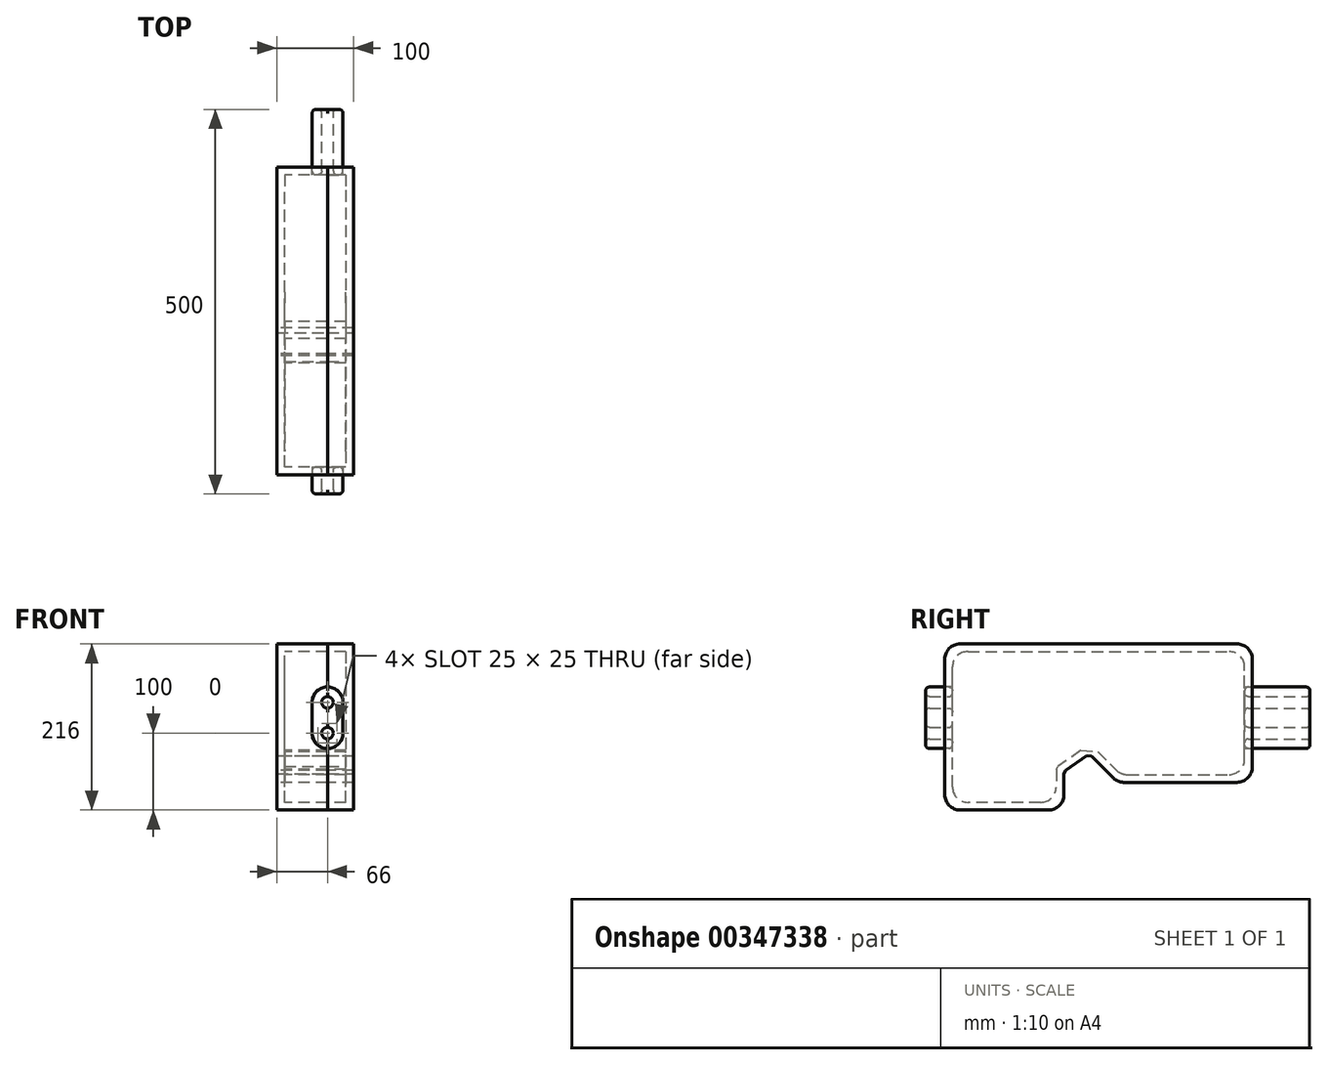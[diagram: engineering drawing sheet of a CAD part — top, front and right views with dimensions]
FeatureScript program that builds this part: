
annotation { "Feature Type Name" : "Feature", "Feature Type Description" : "" }
export const myFeature = defineFeature(function(context is Context, id is Id, definition is map)
    precondition{}
    {
        {
            var Q0;
            Q0=qCreatedBy(makeId("Right.planeOp"),FACE);
            var sketch = newSketch(context, id + "F0", { "sketchPlane" : qUnion([Q0])});
            skLineSegment(sketch, "E0.bottom", {"start": v(200, 75) * mm, "end": v(-200, 75) * mm});
            skLineSegment(sketch, "E0.left", {"start": v(200, 75) * mm, "end": v(200, -75) * mm});
            skLineSegment(sketch, "E0.right", {"start": v(-200, 75) * mm, "end": v(-200, -75) * mm});
            skPoint(sketch, "E0.middle", {"position": v(0, 0) * mm});
            skLineSegment(sketch, "E1", {"start": v(-200, -75) * mm, "end": v(-200, -141) * mm});
            skLineSegment(sketch, "E2", {"start": v(-200, -141) * mm, "end": v(-45, -141) * mm});
            skLineSegment(sketch, "E3", {"start": v(-45, -141) * mm, "end": v(-45, -91) * mm});
            skLineSegment(sketch, "E4", {"start": v(-12.23, -68.06) * mm, "end": v(-87.83, -68.06) * mm, "construction": true});
            skLineSegment(sketch, "E5", {"start": v(200, -75) * mm, "end": v(200, -105) * mm});
            skLineSegment(sketch, "E6", {"start": v(200, -105) * mm, "end": v(25, -105) * mm});
            skLineSegment(sketch, "E7", {"start": v(25, -105) * mm, "end": v(-12.23, -68.06) * mm});
            skLineSegment(sketch, "E8", {"start": v(-45, -91) * mm, "end": v(-12.23, -68.06) * mm});
            skSolve(sketch);
        }
        {
            var Q0;
            Q0=makeQuery(id+"F0.imprint","IMPRINT",FACE,{"disambiguationData":[TD([[makeQuery(id+"F0.imprint","IMPRINT",EDGE,{"derivedFrom":sQuery(id+"F0.wireOp",EDGE,"E0.bottom")}),1.0]])]});
            extrude(context, id + "F1", {"entities" : qUnion([Q0]), "depth" : 100 * mm});
        }
        {
            var Q0;
            Q0=makeQuery(id+"F1.opExtrude","CAP_FACE",FACE,{"disambiguationData":[OSD([sQuery(id+"F0.wireOp",EDGE,"E0.bottom"),sQuery(id+"F0.wireOp",EDGE,"E0.top"),sQuery(id+"F0.wireOp",EDGE,"E0.left"),sQuery(id+"F0.wireOp",EDGE,"E0.right")])],"isStart":true});
            shell(context, id + "F2", {"entities" : qUnion([Q0]), "thickness" : 10 * mm});
        }
        {
            var Q0;
            Q0=makeQuery(id+"F1.opExtrude","SWEPT_FACE",FACE,{"disambiguationData":[OSD([sQuery(id+"F0.wireOp",EDGE,"E0.left")])]});
            var sketch = newSketch(context, id + "F3", { "sketchPlane" : qUnion([Q0])});
            skCircle(sketch, "E9", {"center": v(-66, -41) * mm, "radius": 7.5 * mm});
            skCircle(sketch, "E10", {"center": v(-66, -1) * mm, "radius": 7.5 * mm});
            skLineSegment(sketch, "E11", {"start": v(-66, -1) * mm, "end": v(-66, -41) * mm, "construction": true});
            skLineSegment(sketch, "E12", {"start": v(-66, -1) * mm, "end": v(-100, -1) * mm, "construction": true});
            skSolve(sketch);
        }
        {
            var Q0;
            Q0=qSketchRegion(id+"F3",true);
            extrude(context, id + "F4", {"entities" : qUnion([Q0]), "operationType" : NewBodyOperationType.REMOVE, "oppositeDirection" : true, "depth" : 1000 * mm});
        }
        {
            var Q0;
            Q0=makeQuery(id+"F1.opExtrude","CAP_FACE",FACE,{"disambiguationData":[OSD([sQuery(id+"F0.wireOp",EDGE,"E0.bottom"),sQuery(id+"F0.wireOp",EDGE,"E0.top"),sQuery(id+"F0.wireOp",EDGE,"E0.left"),sQuery(id+"F0.wireOp",EDGE,"E0.right")])],"isStart":true});
            var sketch = newSketch(context, id + "F5", { "sketchPlane" : qUnion([Q0])});
            skLineSegment(sketch, "E13", {"start": v(200, -141) * mm, "end": v(200, 75) * mm});
            skLineSegment(sketch, "E14", {"start": v(200, 75) * mm, "end": v(-200, 75) * mm});
            skLineSegment(sketch, "E15", {"start": v(-200, 75) * mm, "end": v(-200, 75) * mm});
            skLineSegment(sketch, "E16", {"start": v(45, -141) * mm, "end": v(45, -141) * mm});
            skLineSegment(sketch, "E17", {"start": v(45, -141) * mm, "end": v(200, -141) * mm});
            skLineSegment(sketch, "E18", {"start": v(-200, 75) * mm, "end": v(-200, -105) * mm});
            skLineSegment(sketch, "E19", {"start": v(-200, -105) * mm, "end": v(-200, -105) * mm});
            skLineSegment(sketch, "E20", {"start": v(-200, -105) * mm, "end": v(-25, -105) * mm});
            skLineSegment(sketch, "E21", {"start": v(-25, -105) * mm, "end": v(12.23, -68.06) * mm});
            skLineSegment(sketch, "E22", {"start": v(12.23, -68.06) * mm, "end": v(45, -91) * mm});
            skLineSegment(sketch, "E23", {"start": v(45, -91) * mm, "end": v(45, -141) * mm});
            skSolve(sketch);
        }
        {
            var Q0;
            Q0=qSketchRegion(id+"F5",true);
            extrude(context, id + "F6", {"entities" : qUnion([Q0]), "operationType" : NewBodyOperationType.ADD, "oppositeDirection" : true, "depth" : 10 * mm});
        }
        {
            var Q0;
            Q0=makeQuery(id+"F1.opExtrude","SWEPT_FACE",FACE,{"disambiguationData":[OSD([sQuery(id+"F0.wireOp",EDGE,"E2")])]});
            var sketch = newSketch(context, id + "F7", { "sketchPlane" : qUnion([Q0])});
            skLineSegment(sketch, "E24.bottom", {"start": v(65.95, 216.16) * mm, "end": v(66.05, 216.16) * mm});
            skLineSegment(sketch, "E24.top", {"start": v(65.95, -216.16) * mm, "end": v(66.05, -216.16) * mm});
            skLineSegment(sketch, "E24.left", {"start": v(65.95, 216.16) * mm, "end": v(65.95, -216.16) * mm});
            skLineSegment(sketch, "E24.right", {"start": v(66.05, 216.16) * mm, "end": v(66.05, -216.16) * mm});
            skPoint(sketch, "E24.middle", {"position": v(66, 0) * mm});
            skSolve(sketch);
        }
        {
            var Q0;
            Q0=qSketchRegion(id+"F7",true);
            extrude(context, id + "F8", {"entities" : qUnion([Q0]), "operationType" : NewBodyOperationType.REMOVE, "oppositeDirection" : true, "depth" : 1000 * mm});
        }
        {
            var Q0;
            {var subQ0=sQuery(id+"F0.wireOp",EDGE,"E5");var subQ1=sQuery(id+"F0.wireOp",EDGE,"E0.left");var subQ2=makeQuery(id+"F1.opExtrude","SWEPT_FACE",FACE,{"disambiguationData":[OSD([subQ1,subQ0])]});Q0=makeQuery(id+"F8.boolean.opBoolean","SPLIT",FACE,{"disambiguationData":[TD([makeQuery(id+"F8.opExtrude","SWEPT_FACE",FACE,{"disambiguationData":[OSD([sQuery(id+"F7.wireOp",EDGE,"E24.left")])]})])],"derivedFrom":subQ2});}
            var sketch = newSketch(context, id + "F9", { "sketchPlane" : qUnion([Q0])});
            skLineSegment(sketch, "E25", {"start": v(-66, -1) * mm, "end": v(-66, -41) * mm, "construction": true});
            skLineSegment(sketch, "E26", {"start": v(-66, -1) * mm, "end": v(-46, -1) * mm, "construction": true});
            skLineSegment(sketch, "E27", {"start": v(-66, -1) * mm, "end": v(-86, -1) * mm, "construction": true});
            skArc(sketch, "E28", {"start": v(-46, -1) * mm, "mid": v(-66, 19) * mm, "end": v(-86, -1) * mm});
            skArc(sketch, "E29", {"start": v(-86, -41) * mm, "mid": v(-66, -61) * mm, "end": v(-46, -41) * mm});
            skPoint(sketch, "E29.endSnap0", {"position": v(-58.5, -41) * mm});
            skLineSegment(sketch, "E30", {"start": v(-46, -1) * mm, "end": v(-46, -41) * mm});
            skLineSegment(sketch, "E31", {"start": v(-86, -1) * mm, "end": v(-86, -41) * mm});
            skArc(sketch, "E32.0", {"start": v(-45.9, -1) * mm, "mid": v(-66, 19.1) * mm, "end": v(-86.1, -1) * mm});
            skLineSegment(sketch, "E32.1", {"start": v(-45.9, -1) * mm, "end": v(-45.9, -41) * mm});
            skArc(sketch, "E32.2", {"start": v(-86.1, -41) * mm, "mid": v(-66, -61.1) * mm, "end": v(-45.9, -41) * mm});
            skLineSegment(sketch, "E32.3", {"start": v(-86.1, -1) * mm, "end": v(-86.1, -41) * mm});
            skSolve(sketch);
        }
        {
            var Q0;
            Q0 = qSketchRegion(id + "F9", true);
            extrude(context, id + "F10", {"entities" : qUnion([Q0]), "operationType" : NewBodyOperationType.REMOVE, "oppositeDirection" : true, "depth" : 50 * mm});
        }
        {
            var Q0;
            {var subQ0=sQuery(id+"F0.wireOp",EDGE,"E5");var subQ1=sQuery(id+"F0.wireOp",EDGE,"E0.left");var subQ2=makeQuery(id+"F1.opExtrude","SWEPT_FACE",FACE,{"disambiguationData":[OSD([subQ1,subQ0])]});var subQ3=makeQuery(id+"F2.opShell","OFFSET_FACE",FACE,{"disambiguationData":[OSD([subQ1,subQ0])]});Q0=makeQuery(id+"F8.boolean.opBoolean","COPY",FACE,{"disambiguationData":[TD([subQ2,subQ3,makeQuery(id+"F4.boolean.opBoolean","COPY",FACE,{"disambiguationData":[TD([subQ2])],"derivedFrom":makeQuery(id+"F4.opExtrude","SWEPT_FACE",FACE,{"disambiguationData":[OSD([sQuery(id+"F3.wireOp",EDGE,"E9")])]})}),makeQuery(id+"F4.boolean.opBoolean","COPY",FACE,{"disambiguationData":[TD([subQ2])],"derivedFrom":makeQuery(id+"F4.opExtrude","SWEPT_FACE",FACE,{"disambiguationData":[OSD([sQuery(id+"F3.wireOp",EDGE,"E10")])]})})])],"derivedFrom":makeQuery(id+"F8.opExtrude","SWEPT_FACE",FACE,{"disambiguationData":[OSD([sQuery(id+"F7.wireOp",EDGE,"E24.right")])]})});}
            var Q1;
            {var subQ0=sQuery(id+"F0.wireOp",EDGE,"E5");var subQ1=sQuery(id+"F0.wireOp",EDGE,"E0.left");var subQ2=makeQuery(id+"F1.opExtrude","SWEPT_FACE",FACE,{"disambiguationData":[OSD([subQ1,subQ0])]});var subQ3=makeQuery(id+"F2.opShell","OFFSET_FACE",FACE,{"disambiguationData":[OSD([subQ1,subQ0])]});var subQ4=makeQuery(id+"F4.opExtrude","SWEPT_FACE",FACE,{"disambiguationData":[OSD([sQuery(id+"F3.wireOp",EDGE,"E10")])]});var subQ5=makeQuery(id+"F4.boolean.opBoolean","COPY",FACE,{"disambiguationData":[TD([subQ2])],"derivedFrom":subQ4});var subQ6=sQuery(id+"F0.wireOp",EDGE,"E0.bottom");var subQ7=sQuery(id+"F0.wireOp",EDGE,"E1");var subQ8=sQuery(id+"F0.wireOp",EDGE,"E0.right");var subQ9=makeQuery(id+"F1.opExtrude","SWEPT_FACE",FACE,{"disambiguationData":[OSD([subQ8,subQ7])]});var subQ10=makeQuery(id+"F2.opShell","OFFSET_FACE",FACE,{"disambiguationData":[OSD([subQ8,subQ7])]});Q1=makeQuery(id+"F10.boolean.opBoolean","SPLIT",FACE,{"disambiguationData":[TD([makeQuery(id+"F10.opExtrude","SWEPT_FACE",FACE,{"disambiguationData":[OSD([sQuery(id+"F9.wireOp",EDGE,"E28")])]})])],"derivedFrom":makeQuery(id+"F8.boolean.opBoolean","COPY",FACE,{"disambiguationData":[TD([makeQuery(id+"F1.opExtrude","SWEPT_FACE",FACE,{"disambiguationData":[OSD([subQ6])]}),subQ2,subQ9,makeQuery(id+"F2.opShell","OFFSET_FACE",FACE,{"disambiguationData":[OSD([subQ6])]}),subQ3,subQ10,subQ5,makeQuery(id+"F4.boolean.opBoolean","COPY",FACE,{"disambiguationData":[TD([subQ9])],"derivedFrom":subQ4})])],"derivedFrom":makeQuery(id+"F8.opExtrude","SWEPT_FACE",FACE,{"disambiguationData":[OSD([sQuery(id+"F7.wireOp",EDGE,"E24.right")])]})})});}
            var Q2;
            {var subQ0=sQuery(id+"F0.wireOp",EDGE,"E5");var subQ1=sQuery(id+"F0.wireOp",EDGE,"E0.left");var subQ2=makeQuery(id+"F1.opExtrude","SWEPT_FACE",FACE,{"disambiguationData":[OSD([subQ1,subQ0])]});var subQ3=makeQuery(id+"F2.opShell","OFFSET_FACE",FACE,{"disambiguationData":[OSD([subQ1,subQ0])]});var subQ4=makeQuery(id+"F4.opExtrude","SWEPT_FACE",FACE,{"disambiguationData":[OSD([sQuery(id+"F3.wireOp",EDGE,"E9")])]});var subQ5=makeQuery(id+"F4.boolean.opBoolean","COPY",FACE,{"disambiguationData":[TD([subQ2])],"derivedFrom":subQ4});var subQ6=sQuery(id+"F0.wireOp",EDGE,"548lelhJ-FumK-1v7O-jp4s-T3LJ27CFtbea");var subQ7=sQuery(id+"F0.wireOp",EDGE,"E2");var subQ8=sQuery(id+"F0.wireOp",EDGE,"BKIsQGDg-fWEg-7aJj-qOrJ-T1CRB7Qqrcyv");var subQ9=sQuery(id+"F0.wireOp",EDGE,"E1");var subQ10=sQuery(id+"F0.wireOp",EDGE,"E0.right");var subQ11=makeQuery(id+"F2.opShell","OFFSET_FACE",FACE,{"disambiguationData":[OSD([subQ10,subQ9])]});var subQ12=sQuery(id+"F0.wireOp",EDGE,"E6");var subQ13=makeQuery(id+"F1.opExtrude","SWEPT_FACE",FACE,{"disambiguationData":[OSD([subQ10,subQ9])]});var subQ14=sQuery(id+"F0.wireOp",EDGE,"E3");Q2=makeQuery(id+"F10.boolean.opBoolean","SPLIT",FACE,{"disambiguationData":[TD([makeQuery(id+"F10.opExtrude","SWEPT_FACE",FACE,{"disambiguationData":[OSD([sQuery(id+"F9.wireOp",EDGE,"E29")])]})])],"derivedFrom":makeQuery(id+"F8.boolean.opBoolean","COPY",FACE,{"disambiguationData":[TD([subQ2,subQ13,makeQuery(id+"F1.opExtrude","SWEPT_FACE",FACE,{"disambiguationData":[OSD([subQ7])]}),makeQuery(id+"F1.opExtrude","SWEPT_FACE",FACE,{"disambiguationData":[OSD([subQ14])]}),makeQuery(id+"F1.opExtrude","SWEPT_FACE",FACE,{"disambiguationData":[OSD([subQ12])]}),makeQuery(id+"F1.opExtrude","SWEPT_FACE",FACE,{"disambiguationData":[OSD([subQ8])]}),makeQuery(id+"F1.opExtrude","SWEPT_FACE",FACE,{"disambiguationData":[OSD([subQ6])]}),subQ3,subQ11,makeQuery(id+"F2.opShell","OFFSET_FACE",FACE,{"disambiguationData":[OSD([subQ7])]}),makeQuery(id+"F2.opShell","OFFSET_FACE",FACE,{"disambiguationData":[OSD([subQ14])]}),makeQuery(id+"F2.opShell","OFFSET_FACE",FACE,{"disambiguationData":[OSD([subQ12])]}),makeQuery(id+"F2.opShell","OFFSET_FACE",FACE,{"disambiguationData":[OSD([subQ8])]}),makeQuery(id+"F2.opShell","OFFSET_FACE",FACE,{"disambiguationData":[OSD([subQ6])]}),subQ5,makeQuery(id+"F4.boolean.opBoolean","COPY",FACE,{"disambiguationData":[TD([subQ13])],"derivedFrom":subQ4})])],"derivedFrom":makeQuery(id+"F8.opExtrude","SWEPT_FACE",FACE,{"disambiguationData":[OSD([sQuery(id+"F7.wireOp",EDGE,"E24.right")])]})})});}
            extrude(context, id + "F11", {"entities" : qUnion([Q0, Q1, Q2]), "operationType" : NewBodyOperationType.ADD, "depth" : 0.1 * mm});
        }
        {
            var Q0;
            {var subQ1=sQuery(id+"F0.wireOp",EDGE,"E1");var subQ2=sQuery(id+"F0.wireOp",EDGE,"E0.right");var subQ4=makeQuery(id+"F1.opExtrude","SWEPT_FACE",FACE,{"disambiguationData":[OSD([subQ2,subQ1])]});Q0=makeQuery(id+"F8.boolean.opBoolean","SPLIT",FACE,{"disambiguationData":[TD([makeQuery(id+"F8.opExtrude","SWEPT_FACE",FACE,{"disambiguationData":[OSD([sQuery(id+"F7.wireOp",EDGE,"E24.left")])]})])],"derivedFrom":subQ4});}
            var sketch = newSketch(context, id + "F12", { "sketchPlane" : qUnion([Q0])});
            skLineSegment(sketch, "E33", {"start": v(66, -1) * mm, "end": v(66, -41) * mm, "construction": true});
            skLineSegment(sketch, "E34", {"start": v(66, -1) * mm, "end": v(86, -1) * mm, "construction": true});
            skLineSegment(sketch, "E35", {"start": v(66, -1) * mm, "end": v(46, -1) * mm, "construction": true});
            skArc(sketch, "E36", {"start": v(86, -1) * mm, "mid": v(66, 19) * mm, "end": v(46, -1) * mm});
            skArc(sketch, "E37", {"start": v(46, -41) * mm, "mid": v(66, -61) * mm, "end": v(86, -41) * mm});
            skPoint(sketch, "E37.endSnap0", {"position": v(73.5, -41) * mm});
            skLineSegment(sketch, "E38", {"start": v(86, -1) * mm, "end": v(86, -41) * mm});
            skLineSegment(sketch, "E39", {"start": v(46, -1) * mm, "end": v(46, -41) * mm});
            skArc(sketch, "E40.0", {"start": v(86.1, -1) * mm, "mid": v(66, 19.1) * mm, "end": v(45.9, -1) * mm});
            skLineSegment(sketch, "E40.1", {"start": v(86.1, -1) * mm, "end": v(86.1, -41) * mm});
            skArc(sketch, "E40.2", {"start": v(45.9, -41) * mm, "mid": v(66, -61.1) * mm, "end": v(86.1, -41) * mm});
            skLineSegment(sketch, "E40.3", {"start": v(45.9, -1) * mm, "end": v(45.9, -41) * mm});
            skLineSegment(sketch, "E41", {"start": v(66, -41) * mm, "end": v(66, -1) * mm, "construction": true});
            skSolve(sketch);
        }
        {
            var Q0;
            Q0 = qSketchRegion(id + "F12", true);
            extrude(context, id + "F13", {"entities" : qUnion([Q0]), "operationType" : NewBodyOperationType.REMOVE, "oppositeDirection" : true, "depth" : 25 * mm});
        }
        {
            var Q0;
            {var subQ0=sQuery(id+"F0.wireOp",EDGE,"E1");var subQ1=sQuery(id+"F0.wireOp",EDGE,"E0.right");var subQ2=makeQuery(id+"F1.opExtrude","SWEPT_FACE",FACE,{"disambiguationData":[OSD([subQ1,subQ0])]});var subQ3=makeQuery(id+"F2.opShell","OFFSET_FACE",FACE,{"disambiguationData":[OSD([subQ1,subQ0])]});Q0=makeQuery(id+"F8.boolean.opBoolean","COPY",FACE,{"disambiguationData":[TD([subQ2,subQ3,makeQuery(id+"F4.boolean.opBoolean","COPY",FACE,{"disambiguationData":[TD([subQ2])],"derivedFrom":makeQuery(id+"F4.opExtrude","SWEPT_FACE",FACE,{"disambiguationData":[OSD([sQuery(id+"F3.wireOp",EDGE,"E9")])]})}),makeQuery(id+"F4.boolean.opBoolean","COPY",FACE,{"disambiguationData":[TD([subQ2])],"derivedFrom":makeQuery(id+"F4.opExtrude","SWEPT_FACE",FACE,{"disambiguationData":[OSD([sQuery(id+"F3.wireOp",EDGE,"E10")])]})})])],"derivedFrom":makeQuery(id+"F8.opExtrude","SWEPT_FACE",FACE,{"disambiguationData":[OSD([sQuery(id+"F7.wireOp",EDGE,"E24.right")])]})});}
            var Q1;
            {var subQ0=sQuery(id+"F0.wireOp",EDGE,"E1");var subQ1=sQuery(id+"F0.wireOp",EDGE,"E0.right");var subQ2=makeQuery(id+"F1.opExtrude","SWEPT_FACE",FACE,{"disambiguationData":[OSD([subQ1,subQ0])]});var subQ3=makeQuery(id+"F2.opShell","OFFSET_FACE",FACE,{"disambiguationData":[OSD([subQ1,subQ0])]});var subQ4=makeQuery(id+"F4.opExtrude","SWEPT_FACE",FACE,{"disambiguationData":[OSD([sQuery(id+"F3.wireOp",EDGE,"E10")])]});var subQ5=makeQuery(id+"F4.boolean.opBoolean","COPY",FACE,{"disambiguationData":[TD([subQ2])],"derivedFrom":subQ4});var subQ6=sQuery(id+"F0.wireOp",EDGE,"E0.bottom");var subQ7=makeQuery(id+"F2.opShell","OFFSET_FACE",FACE,{"disambiguationData":[OSD([subQ6])]});var subQ8=sQuery(id+"F0.wireOp",EDGE,"E5");var subQ9=sQuery(id+"F0.wireOp",EDGE,"E0.left");var subQ10=makeQuery(id+"F1.opExtrude","SWEPT_FACE",FACE,{"disambiguationData":[OSD([subQ9,subQ8])]});var subQ11=makeQuery(id+"F1.opExtrude","SWEPT_FACE",FACE,{"disambiguationData":[OSD([subQ6])]});var subQ12=makeQuery(id+"F2.opShell","OFFSET_FACE",FACE,{"disambiguationData":[OSD([subQ9,subQ8])]});Q1=makeQuery(id+"F13.boolean.opBoolean","SPLIT",FACE,{"disambiguationData":[TD([makeQuery(id+"F13.opExtrude","SWEPT_FACE",FACE,{"disambiguationData":[OSD([sQuery(id+"F12.wireOp",EDGE,"E36")])]})])],"derivedFrom":makeQuery(id+"F10.boolean.opBoolean","SPLIT",FACE,{"disambiguationData":[TD([subQ11])],"derivedFrom":makeQuery(id+"F8.boolean.opBoolean","COPY",FACE,{"disambiguationData":[TD([subQ11,subQ10,subQ2,subQ7,subQ12,subQ3,makeQuery(id+"F4.boolean.opBoolean","COPY",FACE,{"disambiguationData":[TD([subQ10])],"derivedFrom":subQ4}),subQ5])],"derivedFrom":makeQuery(id+"F8.opExtrude","SWEPT_FACE",FACE,{"disambiguationData":[OSD([sQuery(id+"F7.wireOp",EDGE,"E24.right")])]})})})});}
            var Q2;
            {var subQ0=sQuery(id+"F0.wireOp",EDGE,"E1");var subQ1=sQuery(id+"F0.wireOp",EDGE,"E0.right");var subQ2=makeQuery(id+"F1.opExtrude","SWEPT_FACE",FACE,{"disambiguationData":[OSD([subQ1,subQ0])]});var subQ3=makeQuery(id+"F2.opShell","OFFSET_FACE",FACE,{"disambiguationData":[OSD([subQ1,subQ0])]});var subQ4=makeQuery(id+"F4.opExtrude","SWEPT_FACE",FACE,{"disambiguationData":[OSD([sQuery(id+"F3.wireOp",EDGE,"E9")])]});var subQ5=makeQuery(id+"F4.boolean.opBoolean","COPY",FACE,{"disambiguationData":[TD([subQ2])],"derivedFrom":subQ4});var subQ6=sQuery(id+"F0.wireOp",EDGE,"548lelhJ-FumK-1v7O-jp4s-T3LJ27CFtbea");var subQ7=makeQuery(id+"F1.opExtrude","SWEPT_FACE",FACE,{"disambiguationData":[OSD([subQ6])]});var subQ8=sQuery(id+"F0.wireOp",EDGE,"E2");var subQ9=makeQuery(id+"F2.opShell","OFFSET_FACE",FACE,{"disambiguationData":[OSD([subQ8])]});var subQ10=sQuery(id+"F0.wireOp",EDGE,"BKIsQGDg-fWEg-7aJj-qOrJ-T1CRB7Qqrcyv");var subQ11=makeQuery(id+"F1.opExtrude","SWEPT_FACE",FACE,{"disambiguationData":[OSD([subQ10])]});var subQ12=sQuery(id+"F0.wireOp",EDGE,"E6");var subQ13=makeQuery(id+"F1.opExtrude","SWEPT_FACE",FACE,{"disambiguationData":[OSD([subQ12])]});var subQ14=sQuery(id+"F0.wireOp",EDGE,"E5");var subQ15=sQuery(id+"F0.wireOp",EDGE,"E0.left");var subQ16=makeQuery(id+"F1.opExtrude","SWEPT_FACE",FACE,{"disambiguationData":[OSD([subQ15,subQ14])]});var subQ17=makeQuery(id+"F1.opExtrude","SWEPT_FACE",FACE,{"disambiguationData":[OSD([subQ8])]});var subQ18=makeQuery(id+"F2.opShell","OFFSET_FACE",FACE,{"disambiguationData":[OSD([subQ15,subQ14])]});var subQ19=sQuery(id+"F0.wireOp",EDGE,"E3");var subQ22=makeQuery(id+"F8.opExtrude","SWEPT_FACE",FACE,{"disambiguationData":[OSD([sQuery(id+"F7.wireOp",EDGE,"E24.right")])]});var subQ23=makeQuery(id+"F1.opExtrude","SWEPT_FACE",FACE,{"disambiguationData":[OSD([subQ19])]});var subQ24=makeQuery(id+"F2.opShell","OFFSET_FACE",FACE,{"disambiguationData":[OSD([subQ19])]});var subQ25=makeQuery(id+"F2.opShell","OFFSET_FACE",FACE,{"disambiguationData":[OSD([subQ12])]});var subQ26=makeQuery(id+"F2.opShell","OFFSET_FACE",FACE,{"disambiguationData":[OSD([subQ10])]});var subQ27=makeQuery(id+"F2.opShell","OFFSET_FACE",FACE,{"disambiguationData":[OSD([subQ6])]});Q2=makeQuery(id+"F13.boolean.opBoolean","SPLIT",FACE,{"disambiguationData":[TD([makeQuery(id+"F13.opExtrude","SWEPT_FACE",FACE,{"disambiguationData":[OSD([sQuery(id+"F12.wireOp",EDGE,"E37")])]})])],"derivedFrom":makeQuery(id+"F10.boolean.opBoolean","SPLIT",FACE,{"disambiguationData":[TD([subQ17])],"derivedFrom":makeQuery(id+"F8.boolean.opBoolean","COPY",FACE,{"disambiguationData":[TD([subQ16,subQ2,subQ17,subQ23,subQ13,subQ11,subQ7,subQ18,subQ3,subQ9,subQ24,subQ25,subQ26,subQ27,makeQuery(id+"F4.boolean.opBoolean","COPY",FACE,{"disambiguationData":[TD([subQ16])],"derivedFrom":subQ4}),subQ5])],"derivedFrom":subQ22})})});}
            extrude(context, id + "F14", {"entities" : qUnion([Q0, Q1, Q2]), "operationType" : NewBodyOperationType.ADD, "depth" : 0.1 * mm});
        }
        {
            var Q0;
            {var subQ0=sQuery(id+"F0.wireOp",EDGE,"E7");var subQ1=sQuery(id+"F0.wireOp",EDGE,"E8");Q0=makeQuery(id+"F8.boolean.opBoolean","SPLIT",EDGE,{"disambiguationData":[TD([makeQuery(id+"F8.opExtrude","SWEPT_FACE",FACE,{"disambiguationData":[OSD([sQuery(id+"F7.wireOp",EDGE,"E24.left")])]})])],"derivedFrom":makeQuery(id+"F2.opShell","OFFSET_EDGE",EDGE,{"disambiguationData":[OSD([subQ0,subQ1])]})});}
            var Q1;
            {var subQ0=sQuery(id+"F0.wireOp",EDGE,"E8");var subQ1=sQuery(id+"F0.wireOp",EDGE,"E7");Q1=makeQuery(id+"F8.boolean.opBoolean","SPLIT",EDGE,{"disambiguationData":[TD([makeQuery(id+"F8.opExtrude","SWEPT_FACE",FACE,{"disambiguationData":[OSD([sQuery(id+"F7.wireOp",EDGE,"E24.right")])]})])],"derivedFrom":makeQuery(id+"F2.opShell","OFFSET_EDGE",EDGE,{"disambiguationData":[OSD([subQ1,subQ0])]})});}
            var Q2;
            {var subQ0=sQuery(id+"F0.wireOp",EDGE,"E3");var subQ1=sQuery(id+"F0.wireOp",EDGE,"E8");Q2=makeQuery(id+"F8.boolean.opBoolean","SPLIT",EDGE,{"disambiguationData":[TD([makeQuery(id+"F8.opExtrude","SWEPT_FACE",FACE,{"disambiguationData":[OSD([sQuery(id+"F7.wireOp",EDGE,"E24.left")])]})])],"derivedFrom":makeQuery(id+"F2.opShell","OFFSET_EDGE",EDGE,{"disambiguationData":[OSD([subQ0,subQ1])]})});}
            var Q3;
            {var subQ0=sQuery(id+"F0.wireOp",EDGE,"E8");var subQ1=sQuery(id+"F0.wireOp",EDGE,"E3");Q3=makeQuery(id+"F8.boolean.opBoolean","SPLIT",EDGE,{"disambiguationData":[TD([makeQuery(id+"F8.opExtrude","SWEPT_FACE",FACE,{"disambiguationData":[OSD([sQuery(id+"F7.wireOp",EDGE,"E24.right")])]})])],"derivedFrom":makeQuery(id+"F2.opShell","OFFSET_EDGE",EDGE,{"disambiguationData":[OSD([subQ1,subQ0])]})});}
            var Q4;
            {var subQ0=sQuery(id+"F0.wireOp",EDGE,"E8");var subQ1=sQuery(id+"F0.wireOp",EDGE,"E7");Q4=makeQuery(id+"F8.boolean.opBoolean","SPLIT",EDGE,{"disambiguationData":[TD([makeQuery(id+"F8.opExtrude","SWEPT_FACE",FACE,{"disambiguationData":[OSD([sQuery(id+"F7.wireOp",EDGE,"E24.right")])]})])],"derivedFrom":makeQuery(id+"F1.opExtrude","SWEPT_EDGE",EDGE,{"disambiguationData":[OSD([subQ1,subQ0])]})});}
            var Q5;
            {var subQ0=sQuery(id+"F0.wireOp",EDGE,"E8");var subQ1=sQuery(id+"F0.wireOp",EDGE,"E7");Q5=makeQuery(id+"F8.boolean.opBoolean","SPLIT",EDGE,{"disambiguationData":[TD([makeQuery(id+"F8.opExtrude","SWEPT_FACE",FACE,{"disambiguationData":[OSD([sQuery(id+"F7.wireOp",EDGE,"E24.left")])]})])],"derivedFrom":makeQuery(id+"F1.opExtrude","SWEPT_EDGE",EDGE,{"disambiguationData":[OSD([subQ1,subQ0])]})});}
            var Q6;
            {var subQ0=sQuery(id+"F0.wireOp",EDGE,"E8");var subQ1=sQuery(id+"F0.wireOp",EDGE,"E3");Q6=makeQuery(id+"F8.boolean.opBoolean","SPLIT",EDGE,{"disambiguationData":[TD([makeQuery(id+"F8.opExtrude","SWEPT_FACE",FACE,{"disambiguationData":[OSD([sQuery(id+"F7.wireOp",EDGE,"E24.right")])]})])],"derivedFrom":makeQuery(id+"F1.opExtrude","SWEPT_EDGE",EDGE,{"disambiguationData":[OSD([subQ1,subQ0])]})});}
            var Q7;
            {var subQ0=sQuery(id+"F0.wireOp",EDGE,"E8");var subQ1=sQuery(id+"F0.wireOp",EDGE,"E3");Q7=makeQuery(id+"F8.boolean.opBoolean","SPLIT",EDGE,{"disambiguationData":[TD([makeQuery(id+"F8.opExtrude","SWEPT_FACE",FACE,{"disambiguationData":[OSD([sQuery(id+"F7.wireOp",EDGE,"E24.left")])]})])],"derivedFrom":makeQuery(id+"F1.opExtrude","SWEPT_EDGE",EDGE,{"disambiguationData":[OSD([subQ1,subQ0])]})});}
            chamfer(context, id + "F15", {"entities" : qUnion([Q0, Q1, Q2, Q3, Q4, Q5, Q6, Q7]), "width" : 5 * mm, "tangentPropagation" : true});
        }
        {
            var Q0;
            Q0=makeQuery(id+"F2.opShell","OFFSET_FACE",FACE,{"disambiguationData":[OSD([sQuery(id+"F0.wireOp",EDGE,"E0.bottom"),sQuery(id+"F0.wireOp",EDGE,"E0.left"),sQuery(id+"F0.wireOp",EDGE,"E0.right"),sQuery(id+"F0.wireOp",EDGE,"E1"),sQuery(id+"F0.wireOp",EDGE,"E2"),sQuery(id+"F0.wireOp",EDGE,"E3"),sQuery(id+"F0.wireOp",EDGE,"E5"),sQuery(id+"F0.wireOp",EDGE,"E6"),sQuery(id+"F0.wireOp",EDGE,"E7"),sQuery(id+"F0.wireOp",EDGE,"E8")])]});
            var sketch = newSketch(context, id + "F16", { "sketchPlane" : qUnion([Q0])});
            skLineSegment(sketch, "E42", {"start": v(-5.04, -65.73) * mm, "end": v(35.44, -62.27) * mm});
            skLineSegment(sketch, "E43", {"start": v(-5.04, -65.73) * mm, "end": v(-5.04, -52.1) * mm});
            skLineSegment(sketch, "E44", {"start": v(-5.04, -52.1) * mm, "end": v(32.52, -49.5) * mm});
            skLineSegment(sketch, "E45", {"start": v(32.52, -49.5) * mm, "end": v(35.44, -62.27) * mm});
            skSolve(sketch);
        }
        {
            var Q0;
            Q0 = qSketchRegion(id + "F16", true);
            extrude(context, id + "F17", {"entities" : qUnion([Q0]), "operationType" : NewBodyOperationType.REMOVE, "depth" : 80 * mm});
        }
        {
            var Q0;
            {var subQ0=sQuery(id+"F0.wireOp",EDGE,"E1");var subQ1=sQuery(id+"F0.wireOp",EDGE,"E0.right");var subQ2=makeQuery(id+"F1.opExtrude","SWEPT_FACE",FACE,{"disambiguationData":[OSD([subQ1,subQ0])]});var subQ6=makeQuery(id+"F13.opExtrude","SWEPT_FACE",FACE,{"disambiguationData":[OSD([sQuery(id+"F12.wireOp",EDGE,"E37")])]});var subQ27=sQuery(id+"F7.wireOp",EDGE,"E24.right");var subQ28=makeQuery(id+"F8.opExtrude","SWEPT_FACE",FACE,{"disambiguationData":[OSD([subQ27])]});var subQ30=subQ2;var subQ38=makeQuery(id+"F13.opExtrude","SWEPT_FACE",FACE,{"disambiguationData":[OSD([sQuery(id+"F12.wireOp",EDGE,"E36")])]});var subQ39=makeQuery(id+"F8.opExtrude","SWEPT_FACE",FACE,{"disambiguationData":[OSD([sQuery(id+"F7.wireOp",EDGE,"E24.left")])]});Q0=makeQuery(id+"F14.boolean.opBoolean","MERGE",FACE,{"derivedFrom":[makeQuery(id+"F13.boolean.opBoolean","SPLIT",FACE,{"disambiguationData":[TD([subQ38])],"derivedFrom":makeQuery(id+"F8.boolean.opBoolean","SPLIT",FACE,{"disambiguationData":[TD([subQ39])],"derivedFrom":subQ30})}),makeQuery(id+"F13.boolean.opBoolean","SPLIT",FACE,{"disambiguationData":[TD([subQ38])],"derivedFrom":makeQuery(id+"F8.boolean.opBoolean","SPLIT",FACE,{"disambiguationData":[TD([subQ28])],"derivedFrom":subQ30})}),makeQuery(id+"F14.opExtrude","SWEPT_FACE",FACE,{"disambiguationData":[OSD([subQ1,subQ0,subQ27]),TDD([makeQuery(id+"F8.boolean.opBoolean","INTERSECT",EDGE,{"disambiguationData":[OD(2.0)],"derivedFrom":[subQ30,subQ28]})])]}),makeQuery(id+"F14.opExtrude","SWEPT_FACE",FACE,{"disambiguationData":[OSD([subQ1,subQ0,subQ27]),TDD([makeQuery(id+"F13.boolean.opBoolean","SPLIT",EDGE,{"disambiguationData":[TD([subQ38])],"derivedFrom":makeQuery(id+"F8.boolean.opBoolean","INTERSECT",EDGE,{"disambiguationData":[OD(0.0)],"derivedFrom":[subQ30,subQ28]})})])]}),makeQuery(id+"F14.opExtrude","SWEPT_FACE",FACE,{"disambiguationData":[OSD([subQ1,subQ0,subQ27]),TDD([makeQuery(id+"F13.boolean.opBoolean","SPLIT",EDGE,{"disambiguationData":[TD([subQ6])],"derivedFrom":makeQuery(id+"F8.boolean.opBoolean","INTERSECT",EDGE,{"disambiguationData":[OD(1.0)],"derivedFrom":[subQ30,subQ28]})})])]})]});}
            extrude(context, id + "F18", {"entities" : qUnion([Q0]), "operationType" : NewBodyOperationType.ADD, "depth" : 25 * mm});
        }
        {
            var Q0;
            {var subQ0=sQuery(id+"F0.wireOp",EDGE,"E5");var subQ1=sQuery(id+"F0.wireOp",EDGE,"E0.left");var subQ2=makeQuery(id+"F1.opExtrude","SWEPT_FACE",FACE,{"disambiguationData":[OSD([subQ1,subQ0])]});var subQ26=sQuery(id+"F7.wireOp",EDGE,"E24.right");var subQ27=makeQuery(id+"F8.opExtrude","SWEPT_FACE",FACE,{"disambiguationData":[OSD([subQ26])]});var subQ29=makeQuery(id+"F10.opExtrude","SWEPT_FACE",FACE,{"disambiguationData":[OSD([sQuery(id+"F9.wireOp",EDGE,"E29")])]});var subQ30=subQ2;var subQ33=makeQuery(id+"F10.opExtrude","SWEPT_FACE",FACE,{"disambiguationData":[OSD([sQuery(id+"F9.wireOp",EDGE,"E28")])]});var subQ39=makeQuery(id+"F8.opExtrude","SWEPT_FACE",FACE,{"disambiguationData":[OSD([sQuery(id+"F7.wireOp",EDGE,"E24.left")])]});Q0=makeQuery(id+"F11.boolean.opBoolean","MERGE",FACE,{"derivedFrom":[makeQuery(id+"F10.boolean.opBoolean","SPLIT",FACE,{"disambiguationData":[TD([subQ33])],"derivedFrom":makeQuery(id+"F8.boolean.opBoolean","SPLIT",FACE,{"disambiguationData":[TD([subQ39])],"derivedFrom":subQ30})}),makeQuery(id+"F10.boolean.opBoolean","SPLIT",FACE,{"disambiguationData":[TD([subQ33])],"derivedFrom":makeQuery(id+"F8.boolean.opBoolean","SPLIT",FACE,{"disambiguationData":[TD([subQ27])],"derivedFrom":subQ30})}),makeQuery(id+"F11.opExtrude","SWEPT_FACE",FACE,{"disambiguationData":[OSD([subQ1,subQ0,subQ26]),TDD([makeQuery(id+"F8.boolean.opBoolean","INTERSECT",EDGE,{"disambiguationData":[OD(2.0)],"derivedFrom":[subQ30,subQ27]})])]}),makeQuery(id+"F11.opExtrude","SWEPT_FACE",FACE,{"disambiguationData":[OSD([subQ1,subQ0,subQ26]),TDD([makeQuery(id+"F10.boolean.opBoolean","SPLIT",EDGE,{"disambiguationData":[TD([subQ33])],"derivedFrom":makeQuery(id+"F8.boolean.opBoolean","INTERSECT",EDGE,{"disambiguationData":[OD(0.0)],"derivedFrom":[subQ30,subQ27]})})])]}),makeQuery(id+"F11.opExtrude","SWEPT_FACE",FACE,{"disambiguationData":[OSD([subQ1,subQ0,subQ26]),TDD([makeQuery(id+"F10.boolean.opBoolean","SPLIT",EDGE,{"disambiguationData":[TD([subQ29])],"derivedFrom":makeQuery(id+"F8.boolean.opBoolean","INTERSECT",EDGE,{"disambiguationData":[OD(1.0)],"derivedFrom":[subQ30,subQ27]})})])]})]});}
            extrude(context, id + "F19", {"entities" : qUnion([Q0]), "operationType" : NewBodyOperationType.ADD, "depth" : 75 * mm});
        }
        {
            var Q0;
            {var subQ0=sQuery(id+"F0.wireOp",EDGE,"E1");var subQ1=sQuery(id+"F0.wireOp",EDGE,"E2");Q0=makeQuery(id+"F8.boolean.opBoolean","SPLIT",EDGE,{"disambiguationData":[TD([makeQuery(id+"F8.opExtrude","SWEPT_FACE",FACE,{"disambiguationData":[OSD([sQuery(id+"F7.wireOp",EDGE,"E24.left")])]})])],"derivedFrom":makeQuery(id+"F2.opShell","OFFSET_EDGE",EDGE,{"disambiguationData":[OSD([subQ0,subQ1])]})});}
            var Q1;
            {var subQ0=sQuery(id+"F0.wireOp",EDGE,"E2");var subQ1=sQuery(id+"F0.wireOp",EDGE,"E1");Q1=makeQuery(id+"F8.boolean.opBoolean","SPLIT",EDGE,{"disambiguationData":[TD([makeQuery(id+"F8.opExtrude","SWEPT_FACE",FACE,{"disambiguationData":[OSD([sQuery(id+"F7.wireOp",EDGE,"E24.right")])]})])],"derivedFrom":makeQuery(id+"F2.opShell","OFFSET_EDGE",EDGE,{"disambiguationData":[OSD([subQ1,subQ0])]})});}
            var Q2;
            {var subQ0=sQuery(id+"F0.wireOp",EDGE,"E2");var subQ1=sQuery(id+"F0.wireOp",EDGE,"E1");Q2=makeQuery(id+"F8.boolean.opBoolean","SPLIT",EDGE,{"disambiguationData":[TD([makeQuery(id+"F8.opExtrude","SWEPT_FACE",FACE,{"disambiguationData":[OSD([sQuery(id+"F7.wireOp",EDGE,"E24.left")])]})])],"derivedFrom":makeQuery(id+"F1.opExtrude","SWEPT_EDGE",EDGE,{"disambiguationData":[OSD([subQ1,subQ0])]})});}
            var Q3;
            {var subQ0=sQuery(id+"F0.wireOp",EDGE,"E2");var subQ1=sQuery(id+"F0.wireOp",EDGE,"E1");Q3=makeQuery(id+"F8.boolean.opBoolean","SPLIT",EDGE,{"disambiguationData":[TD([makeQuery(id+"F8.opExtrude","SWEPT_FACE",FACE,{"disambiguationData":[OSD([sQuery(id+"F7.wireOp",EDGE,"E24.right")])]})])],"derivedFrom":makeQuery(id+"F1.opExtrude","SWEPT_EDGE",EDGE,{"disambiguationData":[OSD([subQ1,subQ0])]})});}
            var Q4;
            {var subQ0=sQuery(id+"F0.wireOp",EDGE,"E2");var subQ1=sQuery(id+"F0.wireOp",EDGE,"E3");Q4=makeQuery(id+"F8.boolean.opBoolean","SPLIT",EDGE,{"disambiguationData":[TD([makeQuery(id+"F8.opExtrude","SWEPT_FACE",FACE,{"disambiguationData":[OSD([sQuery(id+"F7.wireOp",EDGE,"E24.left")])]})])],"derivedFrom":makeQuery(id+"F1.opExtrude","SWEPT_EDGE",EDGE,{"disambiguationData":[OSD([subQ0,subQ1])]})});}
            var Q5;
            {var subQ0=sQuery(id+"F0.wireOp",EDGE,"E3");var subQ1=sQuery(id+"F0.wireOp",EDGE,"E2");Q5=makeQuery(id+"F8.boolean.opBoolean","SPLIT",EDGE,{"disambiguationData":[TD([makeQuery(id+"F8.opExtrude","SWEPT_FACE",FACE,{"disambiguationData":[OSD([sQuery(id+"F7.wireOp",EDGE,"E24.right")])]})])],"derivedFrom":makeQuery(id+"F1.opExtrude","SWEPT_EDGE",EDGE,{"disambiguationData":[OSD([subQ1,subQ0])]})});}
            var Q6;
            {var subQ0=sQuery(id+"F0.wireOp",EDGE,"E2");var subQ1=sQuery(id+"F0.wireOp",EDGE,"E3");Q6=makeQuery(id+"F8.boolean.opBoolean","SPLIT",EDGE,{"disambiguationData":[TD([makeQuery(id+"F8.opExtrude","SWEPT_FACE",FACE,{"disambiguationData":[OSD([sQuery(id+"F7.wireOp",EDGE,"E24.left")])]})])],"derivedFrom":makeQuery(id+"F2.opShell","OFFSET_EDGE",EDGE,{"disambiguationData":[OSD([subQ0,subQ1])]})});}
            var Q7;
            {var subQ0=sQuery(id+"F0.wireOp",EDGE,"E3");var subQ1=sQuery(id+"F0.wireOp",EDGE,"E2");Q7=makeQuery(id+"F8.boolean.opBoolean","SPLIT",EDGE,{"disambiguationData":[TD([makeQuery(id+"F8.opExtrude","SWEPT_FACE",FACE,{"disambiguationData":[OSD([sQuery(id+"F7.wireOp",EDGE,"E24.right")])]})])],"derivedFrom":makeQuery(id+"F2.opShell","OFFSET_EDGE",EDGE,{"disambiguationData":[OSD([subQ1,subQ0])]})});}
            var Q8;
            {var subQ0=sQuery(id+"F0.wireOp",EDGE,"E7");var subQ1=sQuery(id+"F0.wireOp",EDGE,"E6");Q8=makeQuery(id+"F8.boolean.opBoolean","SPLIT",EDGE,{"disambiguationData":[TD([makeQuery(id+"F8.opExtrude","SWEPT_FACE",FACE,{"disambiguationData":[OSD([sQuery(id+"F7.wireOp",EDGE,"E24.left")])]})])],"derivedFrom":makeQuery(id+"F1.opExtrude","SWEPT_EDGE",EDGE,{"disambiguationData":[OSD([subQ1,subQ0])]})});}
            var Q9;
            {var subQ0=sQuery(id+"F0.wireOp",EDGE,"E7");var subQ1=sQuery(id+"F0.wireOp",EDGE,"E6");Q9=makeQuery(id+"F8.boolean.opBoolean","SPLIT",EDGE,{"disambiguationData":[TD([makeQuery(id+"F8.opExtrude","SWEPT_FACE",FACE,{"disambiguationData":[OSD([sQuery(id+"F7.wireOp",EDGE,"E24.right")])]})])],"derivedFrom":makeQuery(id+"F1.opExtrude","SWEPT_EDGE",EDGE,{"disambiguationData":[OSD([subQ1,subQ0])]})});}
            var Q10;
            {var subQ0=sQuery(id+"F0.wireOp",EDGE,"E6");var subQ1=sQuery(id+"F0.wireOp",EDGE,"E7");Q10=makeQuery(id+"F8.boolean.opBoolean","SPLIT",EDGE,{"disambiguationData":[TD([makeQuery(id+"F8.opExtrude","SWEPT_FACE",FACE,{"disambiguationData":[OSD([sQuery(id+"F7.wireOp",EDGE,"E24.left")])]})])],"derivedFrom":makeQuery(id+"F2.opShell","OFFSET_EDGE",EDGE,{"disambiguationData":[OSD([subQ0,subQ1])]})});}
            var Q11;
            {var subQ0=sQuery(id+"F0.wireOp",EDGE,"E7");var subQ1=sQuery(id+"F0.wireOp",EDGE,"E6");Q11=makeQuery(id+"F8.boolean.opBoolean","SPLIT",EDGE,{"disambiguationData":[TD([makeQuery(id+"F8.opExtrude","SWEPT_FACE",FACE,{"disambiguationData":[OSD([sQuery(id+"F7.wireOp",EDGE,"E24.right")])]})])],"derivedFrom":makeQuery(id+"F2.opShell","OFFSET_EDGE",EDGE,{"disambiguationData":[OSD([subQ1,subQ0])]})});}
            var Q12;
            {var subQ0=sQuery(id+"F0.wireOp",EDGE,"E6");var subQ1=sQuery(id+"F0.wireOp",EDGE,"E5");Q12=makeQuery(id+"F8.boolean.opBoolean","SPLIT",EDGE,{"disambiguationData":[TD([makeQuery(id+"F8.opExtrude","SWEPT_FACE",FACE,{"disambiguationData":[OSD([sQuery(id+"F7.wireOp",EDGE,"E24.left")])]})])],"derivedFrom":makeQuery(id+"F1.opExtrude","SWEPT_EDGE",EDGE,{"disambiguationData":[OSD([subQ1,subQ0])]})});}
            var Q13;
            {var subQ0=sQuery(id+"F0.wireOp",EDGE,"E6");var subQ1=sQuery(id+"F0.wireOp",EDGE,"E5");Q13=makeQuery(id+"F8.boolean.opBoolean","SPLIT",EDGE,{"disambiguationData":[TD([makeQuery(id+"F8.opExtrude","SWEPT_FACE",FACE,{"disambiguationData":[OSD([sQuery(id+"F7.wireOp",EDGE,"E24.right")])]})])],"derivedFrom":makeQuery(id+"F1.opExtrude","SWEPT_EDGE",EDGE,{"disambiguationData":[OSD([subQ1,subQ0])]})});}
            var Q14;
            {var subQ0=sQuery(id+"F0.wireOp",EDGE,"E5");var subQ1=sQuery(id+"F0.wireOp",EDGE,"E6");Q14=makeQuery(id+"F8.boolean.opBoolean","SPLIT",EDGE,{"disambiguationData":[TD([makeQuery(id+"F8.opExtrude","SWEPT_FACE",FACE,{"disambiguationData":[OSD([sQuery(id+"F7.wireOp",EDGE,"E24.left")])]})])],"derivedFrom":makeQuery(id+"F2.opShell","OFFSET_EDGE",EDGE,{"disambiguationData":[OSD([subQ0,subQ1])]})});}
            var Q15;
            {var subQ0=sQuery(id+"F0.wireOp",EDGE,"E6");var subQ1=sQuery(id+"F0.wireOp",EDGE,"E5");Q15=makeQuery(id+"F8.boolean.opBoolean","SPLIT",EDGE,{"disambiguationData":[TD([makeQuery(id+"F8.opExtrude","SWEPT_FACE",FACE,{"disambiguationData":[OSD([sQuery(id+"F7.wireOp",EDGE,"E24.right")])]})])],"derivedFrom":makeQuery(id+"F2.opShell","OFFSET_EDGE",EDGE,{"disambiguationData":[OSD([subQ1,subQ0])]})});}
            var Q16;
            {var subQ0=sQuery(id+"F0.wireOp",EDGE,"E0.bottom");var subQ1=sQuery(id+"F0.wireOp",EDGE,"E0.left");Q16=makeQuery(id+"F8.boolean.opBoolean","SPLIT",EDGE,{"disambiguationData":[TD([makeQuery(id+"F8.opExtrude","SWEPT_FACE",FACE,{"disambiguationData":[OSD([sQuery(id+"F7.wireOp",EDGE,"E24.left")])]})])],"derivedFrom":makeQuery(id+"F2.opShell","OFFSET_EDGE",EDGE,{"disambiguationData":[OSD([subQ0,subQ1])]})});}
            var Q17;
            {var subQ0=sQuery(id+"F0.wireOp",EDGE,"E0.bottom");var subQ2=sQuery(id+"F0.wireOp",EDGE,"E0.left");Q17=makeQuery(id+"F8.boolean.opBoolean","SPLIT",EDGE,{"disambiguationData":[TD([makeQuery(id+"F8.opExtrude","SWEPT_FACE",FACE,{"disambiguationData":[OSD([sQuery(id+"F7.wireOp",EDGE,"E24.right")])]})])],"derivedFrom":makeQuery(id+"F2.opShell","OFFSET_EDGE",EDGE,{"disambiguationData":[OSD([subQ0,subQ2])]})});}
            var Q18;
            {var subQ0=sQuery(id+"F0.wireOp",EDGE,"E0.bottom");var subQ2=sQuery(id+"F0.wireOp",EDGE,"E0.left");Q18=makeQuery(id+"F8.boolean.opBoolean","SPLIT",EDGE,{"disambiguationData":[TD([makeQuery(id+"F8.opExtrude","SWEPT_FACE",FACE,{"disambiguationData":[OSD([sQuery(id+"F7.wireOp",EDGE,"E24.right")])]})])],"derivedFrom":makeQuery(id+"F1.opExtrude","SWEPT_EDGE",EDGE,{"disambiguationData":[OSD([subQ0,subQ2])]})});}
            var Q19;
            {var subQ0=sQuery(id+"F0.wireOp",EDGE,"E0.bottom");var subQ2=sQuery(id+"F0.wireOp",EDGE,"E0.left");Q19=makeQuery(id+"F8.boolean.opBoolean","SPLIT",EDGE,{"disambiguationData":[TD([makeQuery(id+"F8.opExtrude","SWEPT_FACE",FACE,{"disambiguationData":[OSD([sQuery(id+"F7.wireOp",EDGE,"E24.left")])]})])],"derivedFrom":makeQuery(id+"F1.opExtrude","SWEPT_EDGE",EDGE,{"disambiguationData":[OSD([subQ0,subQ2])]})});}
            var Q20;
            {var subQ0=sQuery(id+"F0.wireOp",EDGE,"E0.bottom");var subQ2=sQuery(id+"F0.wireOp",EDGE,"E0.right");Q20=makeQuery(id+"F8.boolean.opBoolean","SPLIT",EDGE,{"disambiguationData":[TD([makeQuery(id+"F8.opExtrude","SWEPT_FACE",FACE,{"disambiguationData":[OSD([sQuery(id+"F7.wireOp",EDGE,"E24.right")])]})])],"derivedFrom":makeQuery(id+"F1.opExtrude","SWEPT_EDGE",EDGE,{"disambiguationData":[OSD([subQ0,subQ2])]})});}
            var Q21;
            {var subQ0=sQuery(id+"F0.wireOp",EDGE,"E0.bottom");var subQ2=sQuery(id+"F0.wireOp",EDGE,"E0.right");Q21=makeQuery(id+"F8.boolean.opBoolean","SPLIT",EDGE,{"disambiguationData":[TD([makeQuery(id+"F8.opExtrude","SWEPT_FACE",FACE,{"disambiguationData":[OSD([sQuery(id+"F7.wireOp",EDGE,"E24.left")])]})])],"derivedFrom":makeQuery(id+"F1.opExtrude","SWEPT_EDGE",EDGE,{"disambiguationData":[OSD([subQ0,subQ2])]})});}
            var Q22;
            {var subQ0=sQuery(id+"F0.wireOp",EDGE,"E0.bottom");var subQ2=sQuery(id+"F0.wireOp",EDGE,"E0.right");Q22=makeQuery(id+"F8.boolean.opBoolean","SPLIT",EDGE,{"disambiguationData":[TD([makeQuery(id+"F8.opExtrude","SWEPT_FACE",FACE,{"disambiguationData":[OSD([sQuery(id+"F7.wireOp",EDGE,"E24.right")])]})])],"derivedFrom":makeQuery(id+"F2.opShell","OFFSET_EDGE",EDGE,{"disambiguationData":[OSD([subQ0,subQ2])]})});}
            var Q23;
            {var subQ0=sQuery(id+"F0.wireOp",EDGE,"E0.bottom");var subQ1=sQuery(id+"F0.wireOp",EDGE,"E0.right");Q23=makeQuery(id+"F8.boolean.opBoolean","SPLIT",EDGE,{"disambiguationData":[TD([makeQuery(id+"F8.opExtrude","SWEPT_FACE",FACE,{"disambiguationData":[OSD([sQuery(id+"F7.wireOp",EDGE,"E24.left")])]})])],"derivedFrom":makeQuery(id+"F2.opShell","OFFSET_EDGE",EDGE,{"disambiguationData":[OSD([subQ0,subQ1])]})});}
            fillet(context, id + "F20", {"entities" : qUnion([Q0, Q1, Q2, Q3, Q4, Q5, Q6, Q7, Q8, Q9, Q10, Q11, Q12, Q13, Q14, Q15, Q16, Q17, Q18, Q19, Q20, Q21, Q22, Q23]), "radius" : 20 * mm, "tangentPropagation" : true, "allowEdgeOverflow" : false});
        }
        {
            var Q0;
            Q0=makeQuery(id+"F19.opExtrude","CAP_FACE",FACE,{"disambiguationData":[OSD([sQuery(id+"F0.wireOp",EDGE,"E0.left"),sQuery(id+"F0.wireOp",EDGE,"E5"),sQuery(id+"F7.wireOp",EDGE,"E24.right")])],"isStart":false});
            var Q1;
            {var subQ0=sQuery(id+"F0.wireOp",EDGE,"E5");var subQ1=sQuery(id+"F0.wireOp",EDGE,"E0.left");var subQ2=makeQuery(id+"F2.opShell","OFFSET_FACE",FACE,{"disambiguationData":[OSD([subQ1,subQ0])]});var subQ26=sQuery(id+"F7.wireOp",EDGE,"E24.right");var subQ27=makeQuery(id+"F8.opExtrude","SWEPT_FACE",FACE,{"disambiguationData":[OSD([subQ26])]});var subQ29=makeQuery(id+"F10.opExtrude","SWEPT_FACE",FACE,{"disambiguationData":[OSD([sQuery(id+"F9.wireOp",EDGE,"E29")])]});var subQ30=subQ2;var subQ33=makeQuery(id+"F10.opExtrude","SWEPT_FACE",FACE,{"disambiguationData":[OSD([sQuery(id+"F9.wireOp",EDGE,"E28")])]});var subQ39=makeQuery(id+"F8.opExtrude","SWEPT_FACE",FACE,{"disambiguationData":[OSD([sQuery(id+"F7.wireOp",EDGE,"E24.left")])]});Q1=makeQuery(id+"F11.boolean.opBoolean","MERGE",FACE,{"derivedFrom":[makeQuery(id+"F10.boolean.opBoolean","SPLIT",FACE,{"disambiguationData":[TD([subQ33])],"derivedFrom":makeQuery(id+"F8.boolean.opBoolean","SPLIT",FACE,{"disambiguationData":[TD([subQ27])],"derivedFrom":subQ30})}),makeQuery(id+"F10.boolean.opBoolean","SPLIT",FACE,{"disambiguationData":[TD([subQ33])],"derivedFrom":makeQuery(id+"F8.boolean.opBoolean","SPLIT",FACE,{"disambiguationData":[TD([subQ39])],"derivedFrom":subQ30})}),makeQuery(id+"F11.opExtrude","SWEPT_FACE",FACE,{"disambiguationData":[OSD([subQ1,subQ0,subQ26]),TDD([makeQuery(id+"F8.boolean.opBoolean","INTERSECT",EDGE,{"disambiguationData":[OD(2.0)],"derivedFrom":[subQ30,subQ27]})])]}),makeQuery(id+"F11.opExtrude","SWEPT_FACE",FACE,{"disambiguationData":[OSD([subQ1,subQ0,subQ26]),TDD([makeQuery(id+"F10.boolean.opBoolean","SPLIT",EDGE,{"disambiguationData":[TD([subQ33])],"derivedFrom":makeQuery(id+"F8.boolean.opBoolean","INTERSECT",EDGE,{"disambiguationData":[OD(0.0)],"derivedFrom":[subQ30,subQ27]})})])]}),makeQuery(id+"F11.opExtrude","SWEPT_FACE",FACE,{"disambiguationData":[OSD([subQ1,subQ0,subQ26]),TDD([makeQuery(id+"F10.boolean.opBoolean","SPLIT",EDGE,{"disambiguationData":[TD([subQ29])],"derivedFrom":makeQuery(id+"F8.boolean.opBoolean","INTERSECT",EDGE,{"disambiguationData":[OD(1.0)],"derivedFrom":[subQ30,subQ27]})})])]})]});}
            var Q2;
            {var subQ0=sQuery(id+"F0.wireOp",EDGE,"E1");var subQ1=sQuery(id+"F0.wireOp",EDGE,"E0.right");var subQ2=makeQuery(id+"F2.opShell","OFFSET_FACE",FACE,{"disambiguationData":[OSD([subQ1,subQ0])]});var subQ6=makeQuery(id+"F13.opExtrude","SWEPT_FACE",FACE,{"disambiguationData":[OSD([sQuery(id+"F12.wireOp",EDGE,"E37")])]});var subQ27=sQuery(id+"F7.wireOp",EDGE,"E24.right");var subQ28=makeQuery(id+"F8.opExtrude","SWEPT_FACE",FACE,{"disambiguationData":[OSD([subQ27])]});var subQ30=subQ2;var subQ38=makeQuery(id+"F13.opExtrude","SWEPT_FACE",FACE,{"disambiguationData":[OSD([sQuery(id+"F12.wireOp",EDGE,"E36")])]});var subQ39=makeQuery(id+"F8.opExtrude","SWEPT_FACE",FACE,{"disambiguationData":[OSD([sQuery(id+"F7.wireOp",EDGE,"E24.left")])]});Q2=makeQuery(id+"F14.boolean.opBoolean","MERGE",FACE,{"derivedFrom":[makeQuery(id+"F13.boolean.opBoolean","SPLIT",FACE,{"disambiguationData":[TD([subQ38])],"derivedFrom":makeQuery(id+"F8.boolean.opBoolean","SPLIT",FACE,{"disambiguationData":[TD([subQ28])],"derivedFrom":subQ30})}),makeQuery(id+"F13.boolean.opBoolean","SPLIT",FACE,{"disambiguationData":[TD([subQ38])],"derivedFrom":makeQuery(id+"F8.boolean.opBoolean","SPLIT",FACE,{"disambiguationData":[TD([subQ39])],"derivedFrom":subQ30})}),makeQuery(id+"F14.opExtrude","SWEPT_FACE",FACE,{"disambiguationData":[OSD([subQ1,subQ0,subQ27]),TDD([makeQuery(id+"F8.boolean.opBoolean","INTERSECT",EDGE,{"disambiguationData":[OD(2.0)],"derivedFrom":[subQ30,subQ28]})])]}),makeQuery(id+"F14.opExtrude","SWEPT_FACE",FACE,{"disambiguationData":[OSD([subQ1,subQ0,subQ27]),TDD([makeQuery(id+"F13.boolean.opBoolean","SPLIT",EDGE,{"disambiguationData":[TD([subQ38])],"derivedFrom":makeQuery(id+"F8.boolean.opBoolean","INTERSECT",EDGE,{"disambiguationData":[OD(0.0)],"derivedFrom":[subQ30,subQ28]})})])]}),makeQuery(id+"F14.opExtrude","SWEPT_FACE",FACE,{"disambiguationData":[OSD([subQ1,subQ0,subQ27]),TDD([makeQuery(id+"F13.boolean.opBoolean","SPLIT",EDGE,{"disambiguationData":[TD([subQ6])],"derivedFrom":makeQuery(id+"F8.boolean.opBoolean","INTERSECT",EDGE,{"disambiguationData":[OD(1.0)],"derivedFrom":[subQ30,subQ28]})})])]})]});}
            var Q3;
            Q3=makeQuery(id+"F18.opExtrude","CAP_FACE",FACE,{"disambiguationData":[OSD([sQuery(id+"F0.wireOp",EDGE,"E0.right"),sQuery(id+"F0.wireOp",EDGE,"E1"),sQuery(id+"F7.wireOp",EDGE,"E24.right")])],"isStart":false});
            fillet(context, id + "F21", {"entities" : qUnion([Q0, Q1, Q2, Q3]), "radius" : 5 * mm, "tangentPropagation" : true, "allowEdgeOverflow" : false});
        }
    });
